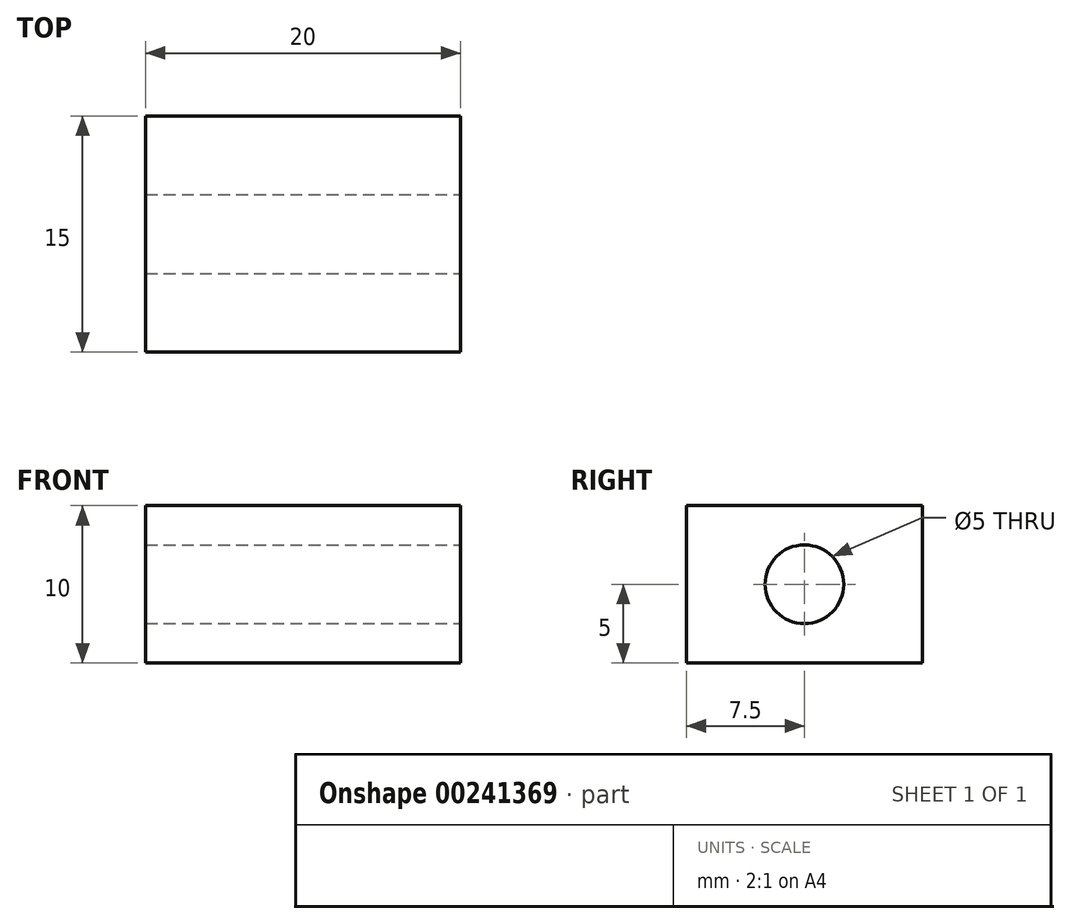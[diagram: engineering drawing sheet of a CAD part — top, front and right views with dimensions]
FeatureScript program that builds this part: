
annotation { "Feature Type Name" : "Feature", "Feature Type Description" : "" }
export const myFeature = defineFeature(function(context is Context, id is Id, definition is map)
    precondition{}
    {
        {
            var Q0;
            Q0=qCreatedBy(makeId("Front.planeOp"),FACE);
            var sketch = newSketch(context, id + "F0", { "sketchPlane" : qUnion([Q0])});
            skLineSegment(sketch, "E0.bottom", {"start": v(-10, 5) * mm, "end": v(10, 5) * mm});
            skLineSegment(sketch, "E0.top", {"start": v(-10, -5) * mm, "end": v(10, -5) * mm});
            skLineSegment(sketch, "E0.left", {"start": v(-10, 5) * mm, "end": v(-10, -5) * mm});
            skLineSegment(sketch, "E0.right", {"start": v(10, 5) * mm, "end": v(10, -5) * mm});
            skPoint(sketch, "E0.middle", {"position": v(0, 0) * mm});
            skSolve(sketch);
        }
        {
            var Q0;
            Q0 = qSketchRegion(id + "F0", true);
            extrude(context, id + "F1", {"entities" : qUnion([Q0]), "depth" : 15 * mm});
        }
        {
            var Q0;
            Q0=makeQuery(id+"F1.opExtrude","SWEPT_FACE",FACE,{"disambiguationData":[OSD([sQuery(id+"F0.wireOp",EDGE,"E0.right")])]});
            var sketch = newSketch(context, id + "F2", { "sketchPlane" : qUnion([Q0])});
            skCircle(sketch, "E1", {"center": v(-7.5, 0) * mm, "radius": 2.5 * mm});
            skPoint(sketch, "E1.centerSnap0", {"position": v(-15, 0) * mm});
            skPoint(sketch, "E1.centerSnap1", {"position": v(-7.5, 5) * mm});
            skSolve(sketch);
        }
        {
            var Q0;
            Q0 = qSketchRegion(id + "F2", true);
            extrude(context, id + "F3", {"entities" : qUnion([Q0]), "operationType" : NewBodyOperationType.REMOVE, "endBound" : BoundingType.THROUGH_ALL, "oppositeDirection" : true, "depth" : 25 * mm});
        }
    });
